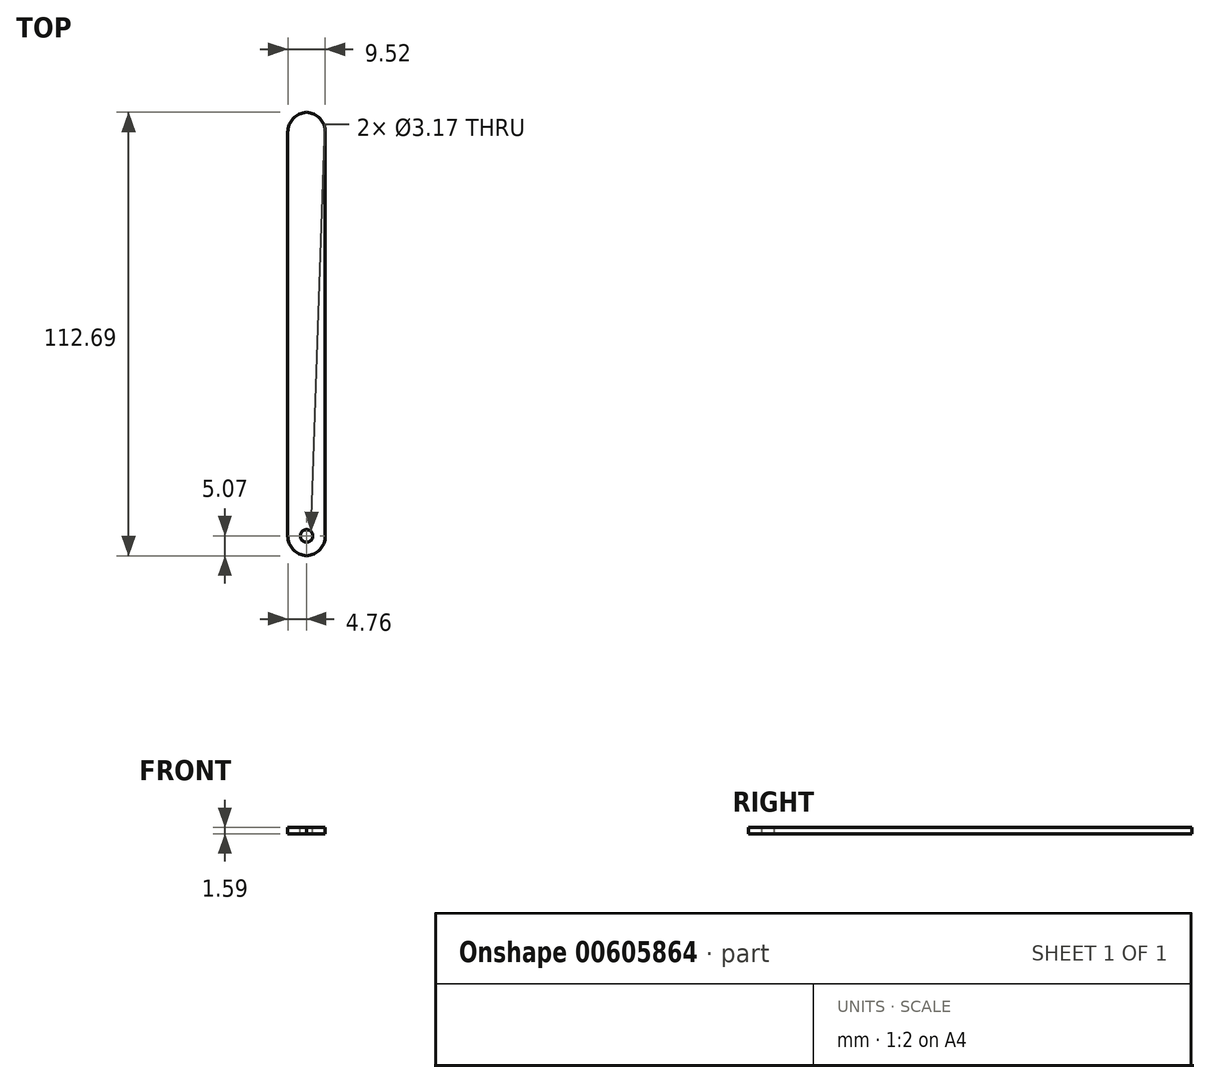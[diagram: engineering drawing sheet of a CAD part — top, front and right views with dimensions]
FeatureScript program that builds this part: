
annotation { "Feature Type Name" : "Feature", "Feature Type Description" : "" }
export const myFeature = defineFeature(function(context is Context, id is Id, definition is map)
    precondition{}
    {
        {
            var Q0;
            Q0=qCreatedBy(makeId("Top.planeOp"),FACE);
            var sketch = newSketch(context, id + "F0", { "sketchPlane" : qUnion([Q0])});
            skLineSegment(sketch, "E0", {"start": v(-4.76, 112.71) * mm, "end": v(-4.76, 0) * mm});
            skLineSegment(sketch, "E1", {"start": v(-4.76, 0) * mm, "end": v(4.76, 0) * mm});
            skLineSegment(sketch, "E2", {"start": v(4.76, 0) * mm, "end": v(4.76, 112.71) * mm});
            skLineSegment(sketch, "E3", {"start": v(-4.76, 112.71) * mm, "end": v(4.76, 112.71) * mm});
            skLineSegment(sketch, "E4.right", {"start": v(4.76, 112.71) * mm, "end": v(4.76, 0) * mm});
            skSolve(sketch);
        }
        {
            var Q0;
            Q0=makeQuery(id+"F0.imprint","IMPRINT",FACE,{"disambiguationData":[TD([[makeQuery(id+"F0.imprint","IMPRINT",EDGE,{"derivedFrom":sQuery(id+"F0.wireOp",EDGE,"E1")}),1.0]])]});
            extrude(context, id + "F1", {"entities" : qUnion([Q0]), "depth" : 1.59 * mm, "offsetDistance" : 25.4 * mm});
        }
        {
            var Q0;
            Q0=makeQuery(id+"F1.opExtrude","SWEPT_EDGE",EDGE,{"disambiguationData":[OSD([sQuery(id+"F0.wireOp",EDGE,"E1"),sQuery(id+"F0.wireOp",EDGE,"E4.right")])]});
            var Q1;
            Q1=makeQuery(id+"F1.opExtrude","SWEPT_EDGE",EDGE,{"disambiguationData":[OSD([sQuery(id+"F0.wireOp",EDGE,"E1"),sQuery(id+"F0.wireOp",EDGE,"E0")])]});
            var Q2;
            Q2=makeQuery(id+"F1.opExtrude","SWEPT_EDGE",EDGE,{"disambiguationData":[OSD([sQuery(id+"F0.wireOp",EDGE,"E3"),sQuery(id+"F0.wireOp",EDGE,"E4.right")])]});
            var Q3;
            Q3=makeQuery(id+"F1.opExtrude","SWEPT_EDGE",EDGE,{"disambiguationData":[OSD([sQuery(id+"F0.wireOp",EDGE,"E3"),sQuery(id+"F0.wireOp",EDGE,"E0")])]});
            fillet(context, id + "F2", {"entities" : qUnion([Q0, Q1, Q2, Q3]), "radius" : 5.08 * mm, "tangentPropagation" : true, "allowEdgeOverflow" : false});
        }
        {
            var Q0;
            Q0=makeQuery(id+"F1.opExtrude","CAP_FACE",FACE,{"disambiguationData":[OSD([sQuery(id+"F0.wireOp",EDGE,"E1"),sQuery(id+"F0.wireOp",EDGE,"E3"),sQuery(id+"F0.wireOp",EDGE,"E0"),sQuery(id+"F0.wireOp",EDGE,"E4.right")])],"isStart":false});
            var sketch = newSketch(context, id + "F3", { "sketchPlane" : qUnion([Q0])});
            skCircle(sketch, "E5", {"center": v(0, 5.08) * mm, "radius": 1.59 * mm});
            skSolve(sketch);
        }
        {
            var Q0;
            Q0=sQuery(id+"F3.wireOp",VERTEX,"E5.center");
            var Q1;
            Q1=makeQuery(id+"F1.opExtrude","SWEPT_BODY",BODY,{"disambiguationData":[OSD([sQuery(id+"F0.wireOp",EDGE,"E1"),sQuery(id+"F0.wireOp",EDGE,"E3"),sQuery(id+"F0.wireOp",EDGE,"E0"),sQuery(id+"F0.wireOp",EDGE,"E4.right")])]});
            hole(context, id + "F4", {"style" : HoleStyle.SIMPLE, "endStyle" : HoleEndStyle.THROUGH, "holeDiameter" : 3.17 * mm, "majorDiameter" : 6.35 * mm, "isTappedThrough" : true, "tappedDepth" : 12.7 * mm, "tapClearance" : 3, "locations" : qUnion([Q0]), "scope" : qUnion([Q1])});
        }
    });
